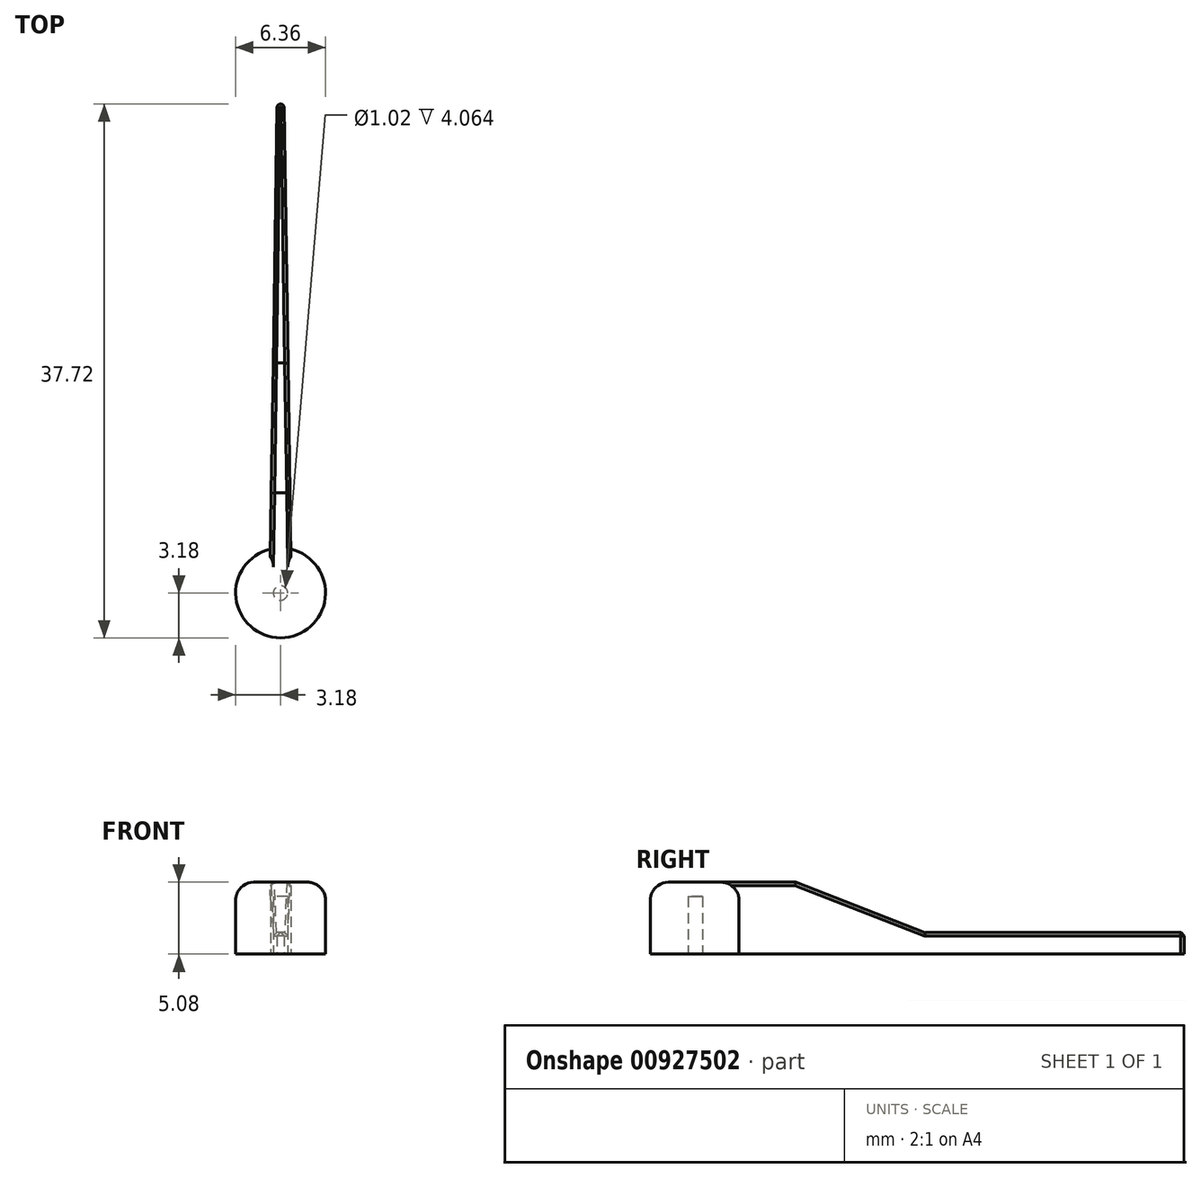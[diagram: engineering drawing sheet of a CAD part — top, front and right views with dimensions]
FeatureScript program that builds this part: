
annotation { "Feature Type Name" : "Feature", "Feature Type Description" : "" }
export const myFeature = defineFeature(function(context is Context, id is Id, definition is map)
    precondition{}
    {
        {
            var Q0;
            Q0=qCreatedBy(makeId("Top.planeOp"),FACE);
            var sketch = newSketch(context, id + "F0", { "sketchPlane" : qUnion([Q0])});
            skLineSegment(sketch, "E0", {"start": v(0, 0) * mm, "end": v(-0.76, 0) * mm});
            skLineSegment(sketch, "E1", {"start": v(0, 0) * mm, "end": v(0.76, 0) * mm});
            skCircle(sketch, "E2", {"center": v(0, 0) * mm, "radius": 3.18 * mm});
            skLineSegment(sketch, "E3", {"start": v(-0.76, 0) * mm, "end": v(-0.25, 34.29) * mm});
            skLineSegment(sketch, "E4", {"start": v(0.76, 0) * mm, "end": v(0.25, 34.29) * mm});
            skLineSegment(sketch, "E5", {"start": v(0.25, 34.29) * mm, "end": v(-0.25, 34.29) * mm});
            skCircle(sketch, "E6", {"center": v(0, 34.29) * mm, "radius": 0.25 * mm});
            skSolve(sketch);
        }
        {
            var Q0;
            Q0=qSketchRegion(id+"F0",true);
            var Q1;
            {var subQ0=sQuery(id+"F0.wireOp",EDGE,"E1");var subQ1=sQuery(id+"F0.wireOp",EDGE,"E0");var subQ2=makeQuery(id+"F0.imprint","INTERSECT",VERTEX,{"derivedFrom":[subQ1,subQ0]});Q1=makeQuery(id+"F0.imprint","IMPRINT",FACE,{"disambiguationData":[TD([[makeQuery(id+"F0.imprint","IMPRINT",EDGE,{"disambiguationData":[TD([[subQ2,-1.0]])],"derivedFrom":subQ1}),-1.0]])]});}
            var Q2;
            {var subQ0=sQuery(id+"F0.wireOp",EDGE,"E1");var subQ1=sQuery(id+"F0.wireOp",EDGE,"E0");var subQ2=makeQuery(id+"F0.imprint","INTERSECT",VERTEX,{"derivedFrom":[subQ1,subQ0]});Q2=makeQuery(id+"F0.imprint","IMPRINT",FACE,{"disambiguationData":[TD([[makeQuery(id+"F0.imprint","IMPRINT",EDGE,{"disambiguationData":[TD([[subQ2,-1.0]])],"derivedFrom":subQ1}),1.0]])]});}
            extrude(context, id + "F1", {"entities" : qUnion([Q0, Q1, Q2]), "depth" : 5.08 * mm, "offsetDistance" : 25.4 * mm});
        }
        {
            var Q0;
            Q0=makeQuery(id+"F1.opExtrude","CAP_EDGE",EDGE,{"disambiguationData":[OSD([sQuery(id+"F0.wireOp",EDGE,"E2")])],"isStart":false});
            fillet(context, id + "F2", {"entities" : qUnion([Q0]), "radius" : 1.27 * mm, "tangentPropagation" : true, "allowEdgeOverflow" : false});
        }
        {
            var Q0;
            Q0=qCreatedBy(makeId("Top.planeOp"),FACE);
            var sketch = newSketch(context, id + "F3", { "sketchPlane" : qUnion([Q0])});
            skCircle(sketch, "E7", {"center": v(0, 0) * mm, "radius": 0.5 * mm});
            skSolve(sketch);
        }
        {
            var Q0;
            Q0=qSketchRegion(id+"F3",true);
            extrude(context, id + "F4", {"entities" : qUnion([Q0]), "operationType" : NewBodyOperationType.REMOVE, "depth" : 4.06 * mm, "offsetDistance" : 25.4 * mm});
        }
        {
            var Q0;
            Q0=qCreatedBy(makeId("Right.planeOp"),FACE);
            var sketch = newSketch(context, id + "F5", { "sketchPlane" : qUnion([Q0])});
            skLineSegment(sketch, "E8", {"start": v(-3.41, 9.15) * mm, "end": v(16.24, 1.52) * mm});
            skLineSegment(sketch, "E9", {"start": v(16.24, 1.52) * mm, "end": v(47.1, 1.52) * mm});
            skLineSegment(sketch, "E10", {"start": v(47.1, 1.52) * mm, "end": v(47.1, 6.88) * mm});
            skLineSegment(sketch, "E11", {"start": v(47.1, 6.88) * mm, "end": v(-3.41, 9.15) * mm});
            skSolve(sketch);
        }
        {
            var Q0;
            Q0=qSketchRegion(id+"F5",true);
            extrude(context, id + "F6", {"entities" : qUnion([Q0]), "operationType" : NewBodyOperationType.REMOVE, "depth" : 5.08 * mm, "offsetDistance" : 25.4 * mm, "hasSecondDirection" : true, "secondDirectionOppositeDirection" : true, "secondDirectionDepth" : 5.08 * mm});
        }
        {
            var Q0;
            Q0=makeQuery(id+"F6.boolean.opBoolean","INTERSECT",EDGE,{"derivedFrom":[makeQuery(id+"F1.opExtrude","SWEPT_FACE",FACE,{"disambiguationData":[OSD([sQuery(id+"F0.wireOp",EDGE,"E3")])]}),makeQuery(id+"F6.opExtrude","SWEPT_FACE",FACE,{"disambiguationData":[OSD([sQuery(id+"F5.wireOp",EDGE,"E9")])]})]});
            var Q1;
            Q1=makeQuery(id+"F6.boolean.opBoolean","INTERSECT",EDGE,{"derivedFrom":[makeQuery(id+"F1.opExtrude","SWEPT_FACE",FACE,{"disambiguationData":[OSD([sQuery(id+"F0.wireOp",EDGE,"E6")])]}),makeQuery(id+"F6.opExtrude","SWEPT_FACE",FACE,{"disambiguationData":[OSD([sQuery(id+"F5.wireOp",EDGE,"E9")])]})]});
            var Q2;
            Q2=makeQuery(id+"F6.boolean.opBoolean","INTERSECT",EDGE,{"derivedFrom":[makeQuery(id+"F1.opExtrude","SWEPT_FACE",FACE,{"disambiguationData":[OSD([sQuery(id+"F0.wireOp",EDGE,"E4")])]}),makeQuery(id+"F6.opExtrude","SWEPT_FACE",FACE,{"disambiguationData":[OSD([sQuery(id+"F5.wireOp",EDGE,"E9")])]})]});
            var Q3;
            Q3=makeQuery(id+"F6.boolean.opBoolean","INTERSECT",EDGE,{"derivedFrom":[makeQuery(id+"F1.opExtrude","SWEPT_FACE",FACE,{"disambiguationData":[OSD([sQuery(id+"F0.wireOp",EDGE,"E4")])]}),makeQuery(id+"F6.opExtrude","SWEPT_FACE",FACE,{"disambiguationData":[OSD([sQuery(id+"F5.wireOp",EDGE,"E8")])]})]});
            var Q4;
            Q4=makeQuery(id+"F6.boolean.opBoolean","INTERSECT",EDGE,{"derivedFrom":[makeQuery(id+"F1.opExtrude","SWEPT_FACE",FACE,{"disambiguationData":[OSD([sQuery(id+"F0.wireOp",EDGE,"E3")])]}),makeQuery(id+"F6.opExtrude","SWEPT_FACE",FACE,{"disambiguationData":[OSD([sQuery(id+"F5.wireOp",EDGE,"E8")])]})]});
            var Q5;
            Q5=makeQuery(id+"F1.opExtrude","CAP_EDGE",EDGE,{"disambiguationData":[OSD([sQuery(id+"F0.wireOp",EDGE,"E3")])],"isStart":false});
            var Q6;
            Q6=makeQuery(id+"F1.opExtrude","CAP_EDGE",EDGE,{"disambiguationData":[OSD([sQuery(id+"F0.wireOp",EDGE,"E4")])],"isStart":false});
            var Q7;
            Q7=makeQuery(id+"F4.boolean.opBoolean","COPY",EDGE,{"derivedFrom":makeQuery(id+"F4.opExtrude","CAP_EDGE",EDGE,{"disambiguationData":[OSD([sQuery(id+"F3.wireOp",EDGE,"E7")])],"isStart":true})});
            chamfer(context, id + "F7", {"entities" : qUnion([Q0, Q1, Q2, Q3, Q4, Q5, Q6, Q7]), "width" : 0.23 * mm, "tangentPropagation" : true});
        }
    });
